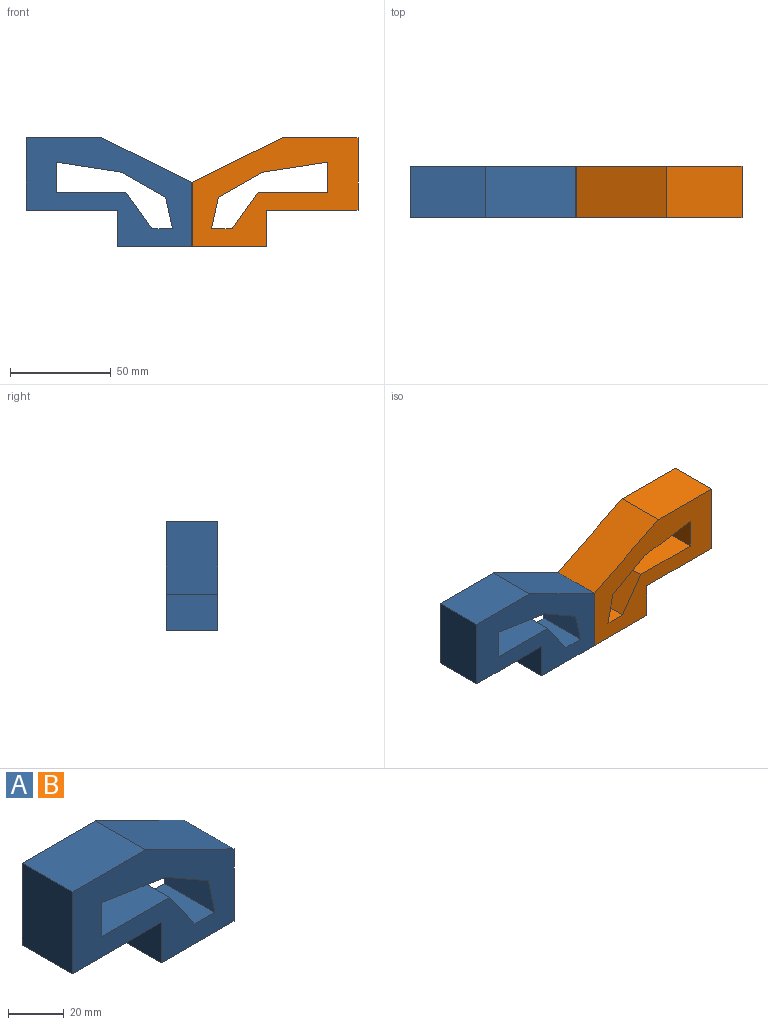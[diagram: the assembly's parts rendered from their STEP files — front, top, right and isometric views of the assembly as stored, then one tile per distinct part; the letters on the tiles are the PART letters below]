
ASSEMBLY  parts=2 mates=1
PART A: 16 faces, bbox 82.2x25.4x53.9 mm
  f0: plane 25.4x14.94mm, normal (1,0,0), area 379.6mm2, adj f1,f13,f14,f15
  f1: plane 32.38x25.4mm, normal (-0.15,0,-0.99), area 832.1mm2, adj f0,f2,f14,f15
  f2: plane 25.4x21.79mm, normal (-0.5,0,-0.87), area 637.5mm2, adj f1,f3,f14,f15
  f3: plane 25.4x15.57mm, normal (-0.98,0,-0.21), area 404.8mm2, adj f2,f4,f14,f15
  f4: plane 25.4x10.27mm, normal (0,0,1), area 261mm2, adj f3,f5,f14,f15
  f5: plane 25.4x18.06mm, normal (0.82,0,0.58), area 561.7mm2, adj f4,f13,f14,f15
  f6: plane 45.45x25.4mm, normal (0,0,-1), area 1154.5mm2, adj f7,f12,f14,f15
  f7: plane 25.4x17.9mm, normal (-1,0,0), area 454.7mm2, adj f6,f8,f14,f15
  f8: plane 36.74x25.4mm, normal (0,0,-1), area 933.1mm2, adj f7,f9,f14,f15
  f9: plane 31.76x25.4mm, normal (1,0,0), area 806.6mm2, adj f8,f10,f14,f15
  f10: plane 44.99x25.4mm, normal (0.44,0,0.9), area 1273.1mm2, adj f9,f11,f14,f15
  f11: plane 37.2x25.4mm, normal (0,0,1), area 945mm2, adj f10,f12,f14,f15
  f12: plane 35.96x25.4mm, normal (-1,0,0), area 913.3mm2, adj f6,f11,f14,f15
  f13: plane 34.56x25.4mm, normal (0,0,1), area 877.7mm2, adj f0,f5,f14,f15
  f14: plane 82.19x53.86mm, normal (0,-1,0), area 2365.6mm2, adj f0,f1,f2,f3,f4,f5,f6,f7
  f15: plane 82.19x53.86mm, normal (0,1,0), area 2365.6mm2, adj f0,f1,f2,f3,f4,f5,f6,f7
PART B: same geometry as A
PLACE A t=(31.84,38.01,17.04)mm
PLACE B rot(axis=(0,0,1),180deg) t=(121.81,38.01,17.04)mm
MATE fastened B.f9 <-> A.f9  axis (-1,0,0) through (76.82,38.01,15.02)mm
